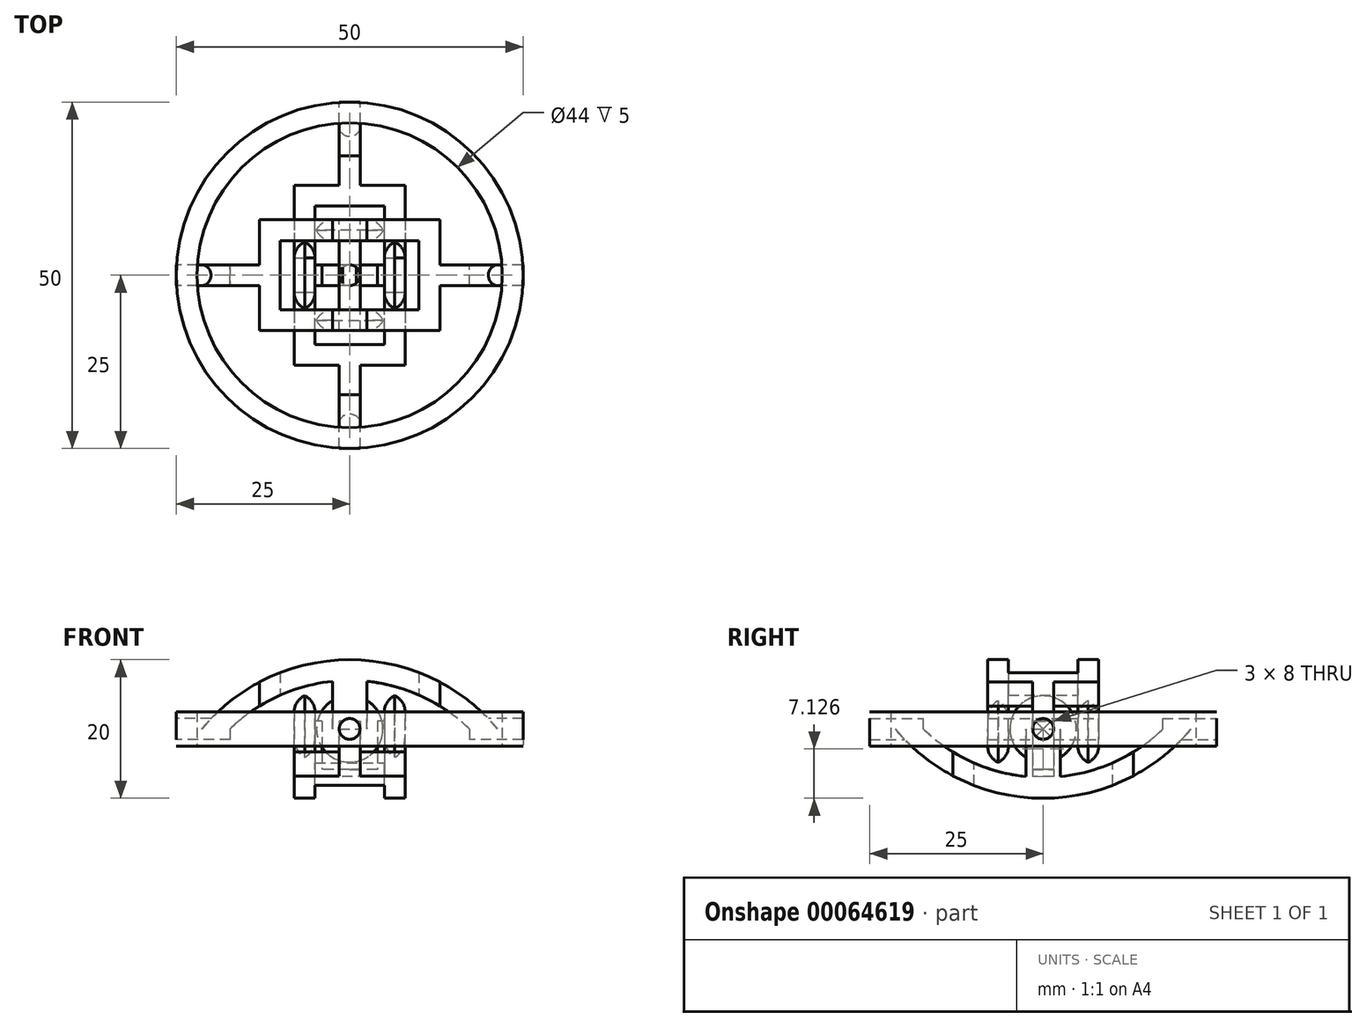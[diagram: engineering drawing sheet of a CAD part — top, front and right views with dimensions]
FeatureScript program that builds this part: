
annotation { "Feature Type Name" : "Feature", "Feature Type Description" : "" }
export const myFeature = defineFeature(function(context is Context, id is Id, definition is map)
    precondition{}
    {
        {
            var Q0;
            Q0=qCreatedBy(makeId("Top.planeOp"),FACE);
            var sketch = newSketch(context, id + "F0", { "sketchPlane" : qUnion([Q0])});
            skLineSegment(sketch, "E0.rect.bottom", {"start": v(10, -5) * mm, "end": v(-10, -5) * mm});
            skLineSegment(sketch, "E0.rect.top", {"start": v(10, 5) * mm, "end": v(-10, 5) * mm});
            skLineSegment(sketch, "E0.rect.left", {"start": v(10, -5) * mm, "end": v(10, 5) * mm});
            skLineSegment(sketch, "E0.rect.right", {"start": v(-10, -5) * mm, "end": v(-10, 5) * mm});
            skPoint(sketch, "E0.rect.middle", {"position": v(0, 0) * mm});
            skLineSegment(sketch, "E1.rect.bottom", {"start": v(-13, 8) * mm, "end": v(13, 8) * mm});
            skLineSegment(sketch, "E1.rect.top", {"start": v(-13, -8) * mm, "end": v(13, -8) * mm});
            skLineSegment(sketch, "E1.rect.left", {"start": v(-13, 8) * mm, "end": v(-13, -8) * mm});
            skLineSegment(sketch, "E1.rect.right", {"start": v(13, 8) * mm, "end": v(13, -8) * mm});
            skLineSegment(sketch, "E2", {"start": v(-13, 1.5) * mm, "end": v(-28, 1.5) * mm});
            skLineSegment(sketch, "E3", {"start": v(-28, 1.5) * mm, "end": v(-28, -1.5) * mm});
            skLineSegment(sketch, "E4", {"start": v(-28, -1.5) * mm, "end": v(-13, -1.5) * mm});
            skLineSegment(sketch, "E5", {"start": v(13, -1.5) * mm, "end": v(28, -1.5) * mm});
            skLineSegment(sketch, "E6", {"start": v(28, -1.5) * mm, "end": v(28, 1.5) * mm});
            skLineSegment(sketch, "E7", {"start": v(28, 1.5) * mm, "end": v(13, 1.5) * mm});
            skSolve(sketch);
        }
        {
            var Q0;
            {var subQ0=sQuery(id+"F0.wireOp",EDGE,"E2");Q0=makeQuery(id+"F0.imprint","IMPRINT",FACE,{"disambiguationData":[TD([[makeQuery(id+"F0.imprint","IMPRINT",EDGE,{"derivedFrom":subQ0}),1.0]])]});}
            var Q1;
            Q1=makeQuery(id+"F0.imprint","IMPRINT",FACE,{"disambiguationData":[TD([[makeQuery(id+"F0.imprint","IMPRINT",EDGE,{"derivedFrom":sQuery(id+"F0.wireOp",EDGE,"E0.rect.bottom")}),1.0]])]});
            var Q2;
            {var subQ0=sQuery(id+"F0.wireOp",EDGE,"E5");Q2=makeQuery(id+"F0.imprint","IMPRINT",FACE,{"disambiguationData":[TD([[makeQuery(id+"F0.imprint","IMPRINT",EDGE,{"derivedFrom":subQ0}),1.0]])]});}
            extrude(context, id + "F1", {"entities" : qUnion([Q0, Q1, Q2]), "endBound" : BoundingType.SYMMETRIC, "depth" : 50 * mm});
        }
        {
            var Q0;
            Q0=qCreatedBy(makeId("Front.planeOp"),FACE);
            var sketch = newSketch(context, id + "F2", { "sketchPlane" : qUnion([Q0])});
            skLineSegment(sketch, "E8", {"start": v(0, 46.34) * mm, "end": v(0, -43.17) * mm});
            skSolve(sketch);
        }
        {
            var Q0;
            Q0=qCreatedBy(makeId("Front.planeOp"),FACE);
            var sketch = newSketch(context, id + "F3", { "sketchPlane" : qUnion([Q0])});
            skCircle(sketch, "E9", {"center": v(0, 0) * mm, "radius": 5 * mm});
            skArc(sketch, "E10", {"start": v(20, 1.5) * mm, "mid": v(10.87, 7.79) * mm, "end": v(0, 10) * mm});
            skArc(sketch, "E11.0", {"start": v(17.26, 0) * mm, "mid": v(10.46, 4.68) * mm, "end": v(2.5, 6.87) * mm});
            skLineSegment(sketch, "E12", {"start": v(25, 1.5) * mm, "end": v(25, 0) * mm});
            skLineSegment(sketch, "E13", {"start": v(20, 1.5) * mm, "end": v(25, 1.5) * mm});
            skLineSegment(sketch, "E14", {"start": v(2.5, 6.87) * mm, "end": v(2.5, 4.33) * mm});
            skLineSegment(sketch, "E15.MirrorCS", {"start": v(-25, 1.5) * mm, "end": v(-25, 0) * mm});
            skArc(sketch, "E16.MirrorCS", {"start": v(-20, 1.5) * mm, "mid": v(-10.87, 7.79) * mm, "end": v(0, 10) * mm});
            skLineSegment(sketch, "E17.MirrorCS", {"start": v(-2.5, 6.87) * mm, "end": v(-2.5, 4.33) * mm});
            skArc(sketch, "E18.MirrorCS", {"start": v(-17.26, 0) * mm, "mid": v(-10.46, 4.68) * mm, "end": v(-2.5, 6.87) * mm});
            skLineSegment(sketch, "E19.MirrorCS", {"start": v(-20, 1.5) * mm, "end": v(-25, 1.5) * mm});
            skLineSegment(sketch, "E20", {"start": v(17.26, 0) * mm, "end": v(17.26, -1.5) * mm});
            skLineSegment(sketch, "E21", {"start": v(17.26, -1.5) * mm, "end": v(25, -1.5) * mm});
            skLineSegment(sketch, "E22", {"start": v(25, -1.5) * mm, "end": v(25, 0) * mm});
            skLineSegment(sketch, "E23", {"start": v(-25, 0) * mm, "end": v(-25, -1.5) * mm});
            skLineSegment(sketch, "E24", {"start": v(-25, -1.5) * mm, "end": v(-17.26, -1.5) * mm});
            skLineSegment(sketch, "E25", {"start": v(-17.26, -1.5) * mm, "end": v(-17.26, 0) * mm});
            skLineSegment(sketch, "E26", {"start": v(0, 10) * mm, "end": v(0, 0) * mm, "construction": true});
            skSolve(sketch);
        }
        {
            var Q0;
            Q0=makeQuery(id+"F3.imprint","IMPRINT",FACE,{"disambiguationData":[TD([[makeQuery(id+"F3.imprint","IMPRINT",EDGE,{"derivedFrom":sQuery(id+"F3.wireOp",EDGE,"E10")}),1.0]])]});
            var Q1;
            {var subQ0=sQuery(id+"F3.wireOp",EDGE,"E9");var subQ1=makeQuery(id+"F3.imprint","INTERSECT",VERTEX,{"derivedFrom":[subQ0,sQuery(id+"F3.wireOp",EDGE,"E14")]});Q1=makeQuery(id+"F3.imprint","IMPRINT",FACE,{"disambiguationData":[TD([[makeQuery(id+"F3.imprint","IMPRINT",EDGE,{"disambiguationData":[TD([[subQ1,-1.0]])],"derivedFrom":subQ0}),1.0]])]});}
            var Q2;
            Q2=makeQuery(id+"F3.imprint","IMPRINT",FACE,{"disambiguationData":[TD([[makeQuery(id+"F3.imprint","IMPRINT",EDGE,{"derivedFrom":sQuery(id+"F3.wireOp",EDGE,"7cc19d34-6d25-45fe-b9ab-7269c0df2a4a4.MirrorCS")}),-1.0]])]});
            var Q3;
            Q3=makeQuery(id+"F3.imprint","IMPRINT",FACE,{"disambiguationData":[TD([[makeQuery(id+"F3.imprint","IMPRINT",EDGE,{"derivedFrom":sQuery(id+"F3.wireOp",EDGE,"Re02jO8j-83i6-SrPj-ZhnU-ibMTVgBzKa9t")}),1.0]])]});
            extrude(context, id + "F4", {"entities" : qUnion([Q0, Q1, Q2, Q3]), "endBound" : BoundingType.THROUGH_ALL, "depth" : 25 * mm, "hasSecondDirection" : true, "secondDirectionBound" : SecondDirectionBoundingType.THROUGH_ALL, "secondDirectionOppositeDirection" : true, "secondDirectionDepth" : 25 * mm});
        }
        {
            var Q0;
            Q0=makeQuery(id+"F1.opExtrude","SWEPT_BODY",BODY,{"disambiguationData":[OSD([sQuery(id+"F0.wireOp",EDGE,"E0.rect.bottom"),sQuery(id+"F0.wireOp",EDGE,"E0.rect.top"),sQuery(id+"F0.wireOp",EDGE,"E0.rect.left"),sQuery(id+"F0.wireOp",EDGE,"E0.rect.right"),sQuery(id+"F0.wireOp",EDGE,"E1.rect.bottom"),sQuery(id+"F0.wireOp",EDGE,"E1.rect.top"),sQuery(id+"F0.wireOp",EDGE,"E1.rect.left"),sQuery(id+"F0.wireOp",EDGE,"E1.rect.right"),sQuery(id+"F0.wireOp",EDGE,"E2"),sQuery(id+"F0.wireOp",EDGE,"E3"),sQuery(id+"F0.wireOp",EDGE,"E4"),sQuery(id+"F0.wireOp",EDGE,"E5"),sQuery(id+"F0.wireOp",EDGE,"E6"),sQuery(id+"F0.wireOp",EDGE,"E7")])]});
            var Q1;
            Q1=makeQuery(id+"F4.opExtrude","SWEPT_BODY",BODY,{"disambiguationData":[OSD([sQuery(id+"F3.wireOp",EDGE,"E9"),sQuery(id+"F3.wireOp",EDGE,"E10"),sQuery(id+"F3.wireOp",EDGE,"E11.0"),sQuery(id+"F3.wireOp",EDGE,"E12"),sQuery(id+"F3.wireOp",EDGE,"Re02jO8j-83i6-SrPj-ZhnU-ibMTVgBzKa9t"),sQuery(id+"F3.wireOp",EDGE,"E13"),sQuery(id+"F3.wireOp",EDGE,"E14"),sQuery(id+"F3.wireOp",EDGE,"E15.MirrorCS"),sQuery(id+"F3.wireOp",EDGE,"E16.MirrorCS"),sQuery(id+"F3.wireOp",EDGE,"E17.MirrorCS"),sQuery(id+"F3.wireOp",EDGE,"E18.MirrorCS"),sQuery(id+"F3.wireOp",EDGE,"7cc19d34-6d25-45fe-b9ab-7269c0df2a4a4.MirrorCS"),sQuery(id+"F3.wireOp",EDGE,"E19.MirrorCS")])]});
            booleanBodies(context, id + "F5", {"operationType" : BooleanOperationType.INTERSECTION, "tools" : qUnion([Q0, Q1])});
        }
        {
            var Q0;
            Q0=makeQuery(id+"F5.opBoolean","INTERSECT",EDGE,{"derivedFrom":[makeQuery(id+"F1.opExtrude","SWEPT_FACE",FACE,{"disambiguationData":[OSD([sQuery(id+"F0.wireOp",EDGE,"E4")])]}),makeQuery(id+"F4.opExtrude","SWEPT_FACE",FACE,{"disambiguationData":[OSD([sQuery(id+"F3.wireOp",EDGE,"E19.MirrorCS")])]})]});
            var Q1;
            Q1=makeQuery(id+"F5.opBoolean","INTERSECT",EDGE,{"derivedFrom":[makeQuery(id+"F1.opExtrude","SWEPT_FACE",FACE,{"disambiguationData":[OSD([sQuery(id+"F0.wireOp",EDGE,"E2")])]}),makeQuery(id+"F4.opExtrude","SWEPT_FACE",FACE,{"disambiguationData":[OSD([sQuery(id+"F3.wireOp",EDGE,"E19.MirrorCS")])]})]});
            var Q2;
            Q2=makeQuery(id+"F5.opBoolean","INTERSECT",EDGE,{"derivedFrom":[makeQuery(id+"F1.opExtrude","SWEPT_FACE",FACE,{"disambiguationData":[OSD([sQuery(id+"F0.wireOp",EDGE,"E4")])]}),makeQuery(id+"F4.opExtrude","SWEPT_FACE",FACE,{"disambiguationData":[OSD([sQuery(id+"F3.wireOp",EDGE,"E24")])]})]});
            var Q3;
            Q3=makeQuery(id+"F5.opBoolean","INTERSECT",EDGE,{"derivedFrom":[makeQuery(id+"F1.opExtrude","SWEPT_FACE",FACE,{"disambiguationData":[OSD([sQuery(id+"F0.wireOp",EDGE,"E2")])]}),makeQuery(id+"F4.opExtrude","SWEPT_FACE",FACE,{"disambiguationData":[OSD([sQuery(id+"F3.wireOp",EDGE,"E24")])]})]});
            var Q4;
            Q4=makeQuery(id+"F5.opBoolean","INTERSECT",EDGE,{"derivedFrom":[makeQuery(id+"F1.opExtrude","SWEPT_FACE",FACE,{"disambiguationData":[OSD([sQuery(id+"F0.wireOp",EDGE,"E7")])]}),makeQuery(id+"F4.opExtrude","SWEPT_FACE",FACE,{"disambiguationData":[OSD([sQuery(id+"F3.wireOp",EDGE,"E13")])]})]});
            var Q5;
            Q5=makeQuery(id+"F5.opBoolean","INTERSECT",EDGE,{"derivedFrom":[makeQuery(id+"F1.opExtrude","SWEPT_FACE",FACE,{"disambiguationData":[OSD([sQuery(id+"F0.wireOp",EDGE,"E7")])]}),makeQuery(id+"F4.opExtrude","SWEPT_FACE",FACE,{"disambiguationData":[OSD([sQuery(id+"F3.wireOp",EDGE,"E21")])]})]});
            var Q6;
            Q6=makeQuery(id+"F5.opBoolean","INTERSECT",EDGE,{"derivedFrom":[makeQuery(id+"F1.opExtrude","SWEPT_FACE",FACE,{"disambiguationData":[OSD([sQuery(id+"F0.wireOp",EDGE,"E5")])]}),makeQuery(id+"F4.opExtrude","SWEPT_FACE",FACE,{"disambiguationData":[OSD([sQuery(id+"F3.wireOp",EDGE,"E21")])]})]});
            var Q7;
            Q7=makeQuery(id+"F5.opBoolean","INTERSECT",EDGE,{"derivedFrom":[makeQuery(id+"F1.opExtrude","SWEPT_FACE",FACE,{"disambiguationData":[OSD([sQuery(id+"F0.wireOp",EDGE,"E5")])]}),makeQuery(id+"F4.opExtrude","SWEPT_FACE",FACE,{"disambiguationData":[OSD([sQuery(id+"F3.wireOp",EDGE,"E13")])]})]});
            fillet(context, id + "F6", {"entities" : qUnion([Q0, Q1, Q2, Q3, Q4, Q5, Q6, Q7]), "radius" : 1.5 * mm, "tangentPropagation" : true, "allowEdgeOverflow" : false});
        }
        {
            var Q0;
            Q0=makeQuery(id+"F8.opPattern","COPY",BODY,{"derivedFrom":makeQuery(id+"F5.opBoolean","INTERSECT",BODY,{"derivedFrom":[makeQuery(id+"F1.opExtrude","SWEPT_BODY",BODY,{"disambiguationData":[OSD([sQuery(id+"F0.wireOp",EDGE,"E0.rect.bottom"),sQuery(id+"F0.wireOp",EDGE,"E0.rect.top"),sQuery(id+"F0.wireOp",EDGE,"E0.rect.left"),sQuery(id+"F0.wireOp",EDGE,"E0.rect.right"),sQuery(id+"F0.wireOp",EDGE,"E1.rect.bottom"),sQuery(id+"F0.wireOp",EDGE,"E1.rect.top"),sQuery(id+"F0.wireOp",EDGE,"E1.rect.left"),sQuery(id+"F0.wireOp",EDGE,"E1.rect.right"),sQuery(id+"F0.wireOp",EDGE,"E2"),sQuery(id+"F0.wireOp",EDGE,"E3"),sQuery(id+"F0.wireOp",EDGE,"E4"),sQuery(id+"F0.wireOp",EDGE,"E5"),sQuery(id+"F0.wireOp",EDGE,"E6"),sQuery(id+"F0.wireOp",EDGE,"E7")])]}),makeQuery(id+"F4.opExtrude","SWEPT_BODY",BODY,{"disambiguationData":[OSD([sQuery(id+"F3.wireOp",EDGE,"2aad1849-a985-4e84-b269-a40025c45bef"),sQuery(id+"F3.wireOp",EDGE,"oUIs2XOa-4Vu7-z26a-mpJD-XDpxixJXROpf"),sQuery(id+"F3.wireOp",EDGE,"nCIHGx5T-ErFx-Tt1R-lAtw-DeMqCE7hFv12"),sQuery(id+"F3.wireOp",EDGE,"2f387838-2f8b-4cff-a27e-d127b03e8324.0"),sQuery(id+"F3.wireOp",EDGE,"2f387838-2f8b-4cff-a27e-d127b03e8324.1"),sQuery(id+"F3.wireOp",EDGE,"2f387838-2f8b-4cff-a27e-d127b03e8324.2"),sQuery(id+"F3.wireOp",EDGE,"2f387838-2f8b-4cff-a27e-d127b03e8324.3"),sQuery(id+"F3.wireOp",EDGE,"2f387838-2f8b-4cff-a27e-d127b03e8324.4")])]})]}),"instanceName":"1"});
            var Q1;
            Q1=makeQuery(id+"F5.opBoolean","INTERSECT",BODY,{"derivedFrom":[makeQuery(id+"F1.opExtrude","SWEPT_BODY",BODY,{"disambiguationData":[OSD([sQuery(id+"F0.wireOp",EDGE,"E0.rect.bottom"),sQuery(id+"F0.wireOp",EDGE,"E0.rect.top"),sQuery(id+"F0.wireOp",EDGE,"E0.rect.left"),sQuery(id+"F0.wireOp",EDGE,"E0.rect.right"),sQuery(id+"F0.wireOp",EDGE,"E1.rect.bottom"),sQuery(id+"F0.wireOp",EDGE,"E1.rect.top"),sQuery(id+"F0.wireOp",EDGE,"E1.rect.left"),sQuery(id+"F0.wireOp",EDGE,"E1.rect.right"),sQuery(id+"F0.wireOp",EDGE,"E2"),sQuery(id+"F0.wireOp",EDGE,"E3"),sQuery(id+"F0.wireOp",EDGE,"E4"),sQuery(id+"F0.wireOp",EDGE,"E5"),sQuery(id+"F0.wireOp",EDGE,"E6"),sQuery(id+"F0.wireOp",EDGE,"E7")])]}),makeQuery(id+"F4.opExtrude","SWEPT_BODY",BODY,{"disambiguationData":[OSD([sQuery(id+"F3.wireOp",EDGE,"E9"),sQuery(id+"F3.wireOp",EDGE,"E10"),sQuery(id+"F3.wireOp",EDGE,"E11.0"),sQuery(id+"F3.wireOp",EDGE,"E12"),sQuery(id+"F3.wireOp",EDGE,"E13"),sQuery(id+"F3.wireOp",EDGE,"E14"),sQuery(id+"F3.wireOp",EDGE,"E15.MirrorCS"),sQuery(id+"F3.wireOp",EDGE,"E16.MirrorCS"),sQuery(id+"F3.wireOp",EDGE,"E17.MirrorCS"),sQuery(id+"F3.wireOp",EDGE,"E18.MirrorCS"),sQuery(id+"F3.wireOp",EDGE,"E19.MirrorCS"),sQuery(id+"F3.wireOp",EDGE,"E20"),sQuery(id+"F3.wireOp",EDGE,"E21"),sQuery(id+"F3.wireOp",EDGE,"E22"),sQuery(id+"F3.wireOp",EDGE,"E23"),sQuery(id+"F3.wireOp",EDGE,"E24"),sQuery(id+"F3.wireOp",EDGE,"E25")])]})]});
            var Q2;
            Q2=qCreatedBy(makeId("Top.planeOp"),FACE);
            mirror(context, id + "F7", {"entities" : qUnion([Q0, Q1]), "mirrorPlane" : qUnion([Q2])});
        }
        {
            var Q0;
            Q0=makeQuery(id+"F7.opPattern","COPY",BODY,{"derivedFrom":makeQuery(id+"F5.opBoolean","INTERSECT",BODY,{"derivedFrom":[makeQuery(id+"F1.opExtrude","SWEPT_BODY",BODY,{"disambiguationData":[OSD([sQuery(id+"F0.wireOp",EDGE,"E0.rect.bottom"),sQuery(id+"F0.wireOp",EDGE,"E0.rect.top"),sQuery(id+"F0.wireOp",EDGE,"E0.rect.left"),sQuery(id+"F0.wireOp",EDGE,"E0.rect.right"),sQuery(id+"F0.wireOp",EDGE,"E1.rect.bottom"),sQuery(id+"F0.wireOp",EDGE,"E1.rect.top"),sQuery(id+"F0.wireOp",EDGE,"E1.rect.left"),sQuery(id+"F0.wireOp",EDGE,"E1.rect.right"),sQuery(id+"F0.wireOp",EDGE,"E2"),sQuery(id+"F0.wireOp",EDGE,"E3"),sQuery(id+"F0.wireOp",EDGE,"E4"),sQuery(id+"F0.wireOp",EDGE,"E5"),sQuery(id+"F0.wireOp",EDGE,"E6"),sQuery(id+"F0.wireOp",EDGE,"E7")])]}),makeQuery(id+"F4.opExtrude","SWEPT_BODY",BODY,{"disambiguationData":[OSD([sQuery(id+"F3.wireOp",EDGE,"E9"),sQuery(id+"F3.wireOp",EDGE,"E10"),sQuery(id+"F3.wireOp",EDGE,"E11.0"),sQuery(id+"F3.wireOp",EDGE,"E12"),sQuery(id+"F3.wireOp",EDGE,"E13"),sQuery(id+"F3.wireOp",EDGE,"E14"),sQuery(id+"F3.wireOp",EDGE,"E15.MirrorCS"),sQuery(id+"F3.wireOp",EDGE,"E16.MirrorCS"),sQuery(id+"F3.wireOp",EDGE,"E17.MirrorCS"),sQuery(id+"F3.wireOp",EDGE,"E18.MirrorCS"),sQuery(id+"F3.wireOp",EDGE,"E19.MirrorCS"),sQuery(id+"F3.wireOp",EDGE,"E20"),sQuery(id+"F3.wireOp",EDGE,"E21"),sQuery(id+"F3.wireOp",EDGE,"E22"),sQuery(id+"F3.wireOp",EDGE,"E23"),sQuery(id+"F3.wireOp",EDGE,"E24"),sQuery(id+"F3.wireOp",EDGE,"E25")])]})]}),"instanceName":"1"});
            var Q1;
            Q1=sQuery(id+"F2.wireOp",EDGE,"E8");
            transform(context, id + "F8", {"entities" : qUnion([Q0]), "transformType" : TransformType.ROTATION, "transformAxis" : qUnion([Q1]), "angle" : 90 * degree, "makeCopy" : false});
        }
        {
            var Q0;
            Q0=makeQuery(id+"F7.opPattern","COPY",FACE,{"derivedFrom":makeQuery(id+"F4.opExtrude","SWEPT_FACE",FACE,{"disambiguationData":[OSD([sQuery(id+"F3.wireOp",EDGE,"E15.MirrorCS"),sQuery(id+"F3.wireOp",EDGE,"E23")])]}),"instanceName":"1"});
            var Q1;
            Q1=makeQuery(id+"F1.opExtrude","SWEPT_FACE",FACE,{"disambiguationData":[OSD([sQuery(id+"F0.wireOp",EDGE,"E1.rect.top")])]});
            var Q2;
            Q2=makeQuery(id+"F1.opExtrude","SWEPT_FACE",FACE,{"disambiguationData":[OSD([sQuery(id+"F0.wireOp",EDGE,"E1.rect.bottom")])]});
            extrude(context, id + "F9", {"entities" : qUnion([Q0]), "endBound" : BoundingType.UP_TO_SURFACE, "oppositeDirection" : true, "endBoundEntityFace" : qUnion([Q1]), "depth" : 25 * mm, "hasSecondDirection" : true, "secondDirectionBound" : SecondDirectionBoundingType.UP_TO_SURFACE, "secondDirectionOppositeDirection" : true, "secondDirectionBoundEntityFace" : qUnion([Q2]), "secondDirectionDepth" : 25 * mm});
        }
        {
            var Q0;
            {var subQ0=sQuery(id+"F3.wireOp",EDGE,"E11.0");var subQ1=sQuery(id+"F3.wireOp",EDGE,"E14");Q0=makeQuery(id+"F7.opPattern","COPY",EDGE,{"derivedFrom":makeQuery(id+"F5.opBoolean","SPLIT",EDGE,{"disambiguationData":[TD([makeQuery(id+"F1.opExtrude","SWEPT_FACE",FACE,{"disambiguationData":[OSD([sQuery(id+"F0.wireOp",EDGE,"E0.rect.top")])]})])],"derivedFrom":makeQuery(id+"F4.opExtrude","SWEPT_EDGE",EDGE,{"disambiguationData":[OSD([subQ0,subQ1])]})}),"instanceName":"1"});}
            cPlane(context, id + "F10", {"entities" : qUnion([Q0]), "cplaneType" : CPlaneType.LINE_ANGLE, "offset" : 150 * mm, "angle" : 90 * degree, "width" : 150 * mm, "height" : 150 * mm});
        }
        {
            var Q0;
            Q0=qCreatedBy(id+"F10.planeOp",FACE);
            var sketch = newSketch(context, id + "F11", { "sketchPlane" : qUnion([Q0])});
            skCircle(sketch, "E27", {"center": v(0, 0) * mm, "radius": 1.5 * mm});
            skLineSegment(sketch, "E28.rect.bottom", {"start": v(5, 1.5) * mm, "end": v(-5, 1.5) * mm});
            skLineSegment(sketch, "E28.rect.top", {"start": v(5, -1.5) * mm, "end": v(-5, -1.5) * mm});
            skLineSegment(sketch, "E28.rect.left", {"start": v(5, 1.5) * mm, "end": v(5, -1.5) * mm});
            skLineSegment(sketch, "E28.rect.right", {"start": v(-5, 1.5) * mm, "end": v(-5, -1.5) * mm});
            skLineSegment(sketch, "E29", {"start": v(-4, -1.5) * mm, "end": v(-4, 1.5) * mm});
            skLineSegment(sketch, "E30", {"start": v(4, 1.5) * mm, "end": v(4, -1.5) * mm});
            skSolve(sketch);
        }
        {
            var Q0;
            {var subQ0=sQuery(id+"F11.wireOp",EDGE,"E28.rect.left");Q0=makeQuery(id+"F11.imprint","IMPRINT",FACE,{"disambiguationData":[TD([[makeQuery(id+"F11.imprint","IMPRINT",EDGE,{"derivedFrom":subQ0}),-1.0]])]});}
            var Q1;
            {var subQ0=sQuery(id+"F11.wireOp",EDGE,"E27");var subQ1=makeQuery(id+"F11.imprint","INTERSECT",VERTEX,{"derivedFrom":[subQ0,sQuery(id+"F11.wireOp",EDGE,"E28.rect.bottom")]});Q1=makeQuery(id+"F11.imprint","IMPRINT",FACE,{"disambiguationData":[TD([[makeQuery(id+"F11.imprint","IMPRINT",EDGE,{"disambiguationData":[TD([[subQ1,-1.0]])],"derivedFrom":subQ0}),1.0]])]});}
            var Q2;
            {var subQ0=sQuery(id+"F11.wireOp",EDGE,"E28.rect.right");Q2=makeQuery(id+"F11.imprint","IMPRINT",FACE,{"disambiguationData":[TD([[makeQuery(id+"F11.imprint","IMPRINT",EDGE,{"derivedFrom":subQ0}),1.0]])]});}
            var Q3;
            {var subQ5=sQuery(id+"F11.wireOp",EDGE,"E30");Q3=makeQuery(id+"F11.imprint","IMPRINT",FACE,{"disambiguationData":[TD([[makeQuery(id+"F11.imprint","IMPRINT",EDGE,{"derivedFrom":subQ5}),-1.0]])]});}
            var Q4;
            {var subQ5=sQuery(id+"F11.wireOp",EDGE,"E29");Q4=makeQuery(id+"F11.imprint","IMPRINT",FACE,{"disambiguationData":[TD([[makeQuery(id+"F11.imprint","IMPRINT",EDGE,{"derivedFrom":subQ5}),-1.0]])]});}
            extrude(context, id + "F12", {"entities" : qUnion([Q0, Q1, Q2, Q3, Q4]), "depth" : 1 * mm});
        }
        {
            var Q0;
            {var subQ0=sQuery(id+"F11.wireOp",EDGE,"E27");var subQ1=makeQuery(id+"F11.imprint","INTERSECT",VERTEX,{"derivedFrom":[subQ0,sQuery(id+"F11.wireOp",EDGE,"E28.rect.bottom")]});Q0=makeQuery(id+"F11.imprint","IMPRINT",FACE,{"disambiguationData":[TD([[makeQuery(id+"F11.imprint","IMPRINT",EDGE,{"disambiguationData":[TD([[subQ1,-1.0]])],"derivedFrom":subQ0}),1.0]])]});}
            var Q1;
            {var subQ0=sQuery(id+"F11.wireOp",EDGE,"E28.rect.right");Q1=makeQuery(id+"F11.imprint","IMPRINT",FACE,{"disambiguationData":[TD([[makeQuery(id+"F11.imprint","IMPRINT",EDGE,{"derivedFrom":subQ0}),1.0]])]});}
            var Q2;
            {var subQ0=sQuery(id+"F11.wireOp",EDGE,"E28.rect.left");Q2=makeQuery(id+"F11.imprint","IMPRINT",FACE,{"disambiguationData":[TD([[makeQuery(id+"F11.imprint","IMPRINT",EDGE,{"derivedFrom":subQ0}),-1.0]])]});}
            var Q3;
            Q3=makeQuery(id+"F9.opExtrude","SWEPT_FACE",FACE,{"disambiguationData":[OSD([sQuery(id+"F0.wireOp",EDGE,"E2"),sQuery(id+"F3.wireOp",EDGE,"E15.MirrorCS"),sQuery(id+"F3.wireOp",EDGE,"E23"),sQuery(id+"F3.wireOp",EDGE,"E24")])]});
            var Q4;
            Q4=makeQuery(id+"F9.opExtrude","SWEPT_BODY",BODY,{"disambiguationData":[OSD([sQuery(id+"F3.wireOp",EDGE,"E15.MirrorCS"),sQuery(id+"F3.wireOp",EDGE,"E23")])]});
            extrude(context, id + "F13", {"entities" : qUnion([Q0, Q1, Q2]), "operationType" : NewBodyOperationType.ADD, "endBoundEntityFace" : qUnion([Q3]), "endBoundEntityBody" : qUnion([Q4]), "depth" : 8 * mm});
        }
        {
            var Q0;
            Q0=qCreatedBy(makeId("Top.planeOp"),FACE);
            var sketch = newSketch(context, id + "F14", { "sketchPlane" : qUnion([Q0])});
            skCircle(sketch, "E31", {"center": v(0, 0) * mm, "radius": 25 * mm});
            skCircle(sketch, "E32.0", {"center": v(0, 0) * mm, "radius": 22 * mm});
            skSolve(sketch);
        }
        {
            var Q0;
            Q0=makeQuery(id+"F14.imprint","IMPRINT",FACE,{"disambiguationData":[TD([[makeQuery(id+"F14.imprint","IMPRINT",EDGE,{"derivedFrom":sQuery(id+"F14.wireOp",EDGE,"E31")}),1.0]])]});
            extrude(context, id + "F15", {"entities" : qUnion([Q0]), "endBound" : BoundingType.SYMMETRIC, "depth" : 5 * mm});
        }
        {
            var Q0;
            Q0=makeQuery(id+"F7.opPattern","COPY",EDGE,{"derivedFrom":makeQuery(id+"F5.opBoolean","INTERSECT",EDGE,{"derivedFrom":[makeQuery(id+"F1.opExtrude","SWEPT_FACE",FACE,{"disambiguationData":[OSD([sQuery(id+"F0.wireOp",EDGE,"E0.rect.bottom")])]}),makeQuery(id+"F4.opExtrude","SWEPT_FACE",FACE,{"disambiguationData":[OSD([sQuery(id+"F3.wireOp",EDGE,"E9")])]})]}),"instanceName":"1"});
            var Q1;
            Q1=makeQuery(id+"F7.opPattern","COPY",EDGE,{"derivedFrom":makeQuery(id+"F5.opBoolean","INTERSECT",EDGE,{"derivedFrom":[makeQuery(id+"F1.opExtrude","SWEPT_FACE",FACE,{"disambiguationData":[OSD([sQuery(id+"F0.wireOp",EDGE,"E0.rect.top")])]}),makeQuery(id+"F4.opExtrude","SWEPT_FACE",FACE,{"disambiguationData":[OSD([sQuery(id+"F3.wireOp",EDGE,"E9")])]})]}),"instanceName":"1"});
            var Q2;
            Q2=makeQuery(id+"F5.opBoolean","INTERSECT",EDGE,{"derivedFrom":[makeQuery(id+"F1.opExtrude","SWEPT_FACE",FACE,{"disambiguationData":[OSD([sQuery(id+"F0.wireOp",EDGE,"E0.rect.bottom")])]}),makeQuery(id+"F4.opExtrude","SWEPT_FACE",FACE,{"disambiguationData":[OSD([sQuery(id+"F3.wireOp",EDGE,"E9")])]})]});
            var Q3;
            Q3=makeQuery(id+"F5.opBoolean","INTERSECT",EDGE,{"derivedFrom":[makeQuery(id+"F1.opExtrude","SWEPT_FACE",FACE,{"disambiguationData":[OSD([sQuery(id+"F0.wireOp",EDGE,"E0.rect.top")])]}),makeQuery(id+"F4.opExtrude","SWEPT_FACE",FACE,{"disambiguationData":[OSD([sQuery(id+"F3.wireOp",EDGE,"E9")])]})]});
            var Q4;
            Q4=makeQuery(id+"F5.opBoolean","INTERSECT",EDGE,{"derivedFrom":[makeQuery(id+"F1.opExtrude","SWEPT_FACE",FACE,{"disambiguationData":[OSD([sQuery(id+"F0.wireOp",EDGE,"E1.rect.top")])]}),makeQuery(id+"F4.opExtrude","SWEPT_FACE",FACE,{"disambiguationData":[OSD([sQuery(id+"F3.wireOp",EDGE,"E9")])]})]});
            var Q5;
            Q5=makeQuery(id+"F7.opPattern","COPY",EDGE,{"derivedFrom":makeQuery(id+"F5.opBoolean","INTERSECT",EDGE,{"derivedFrom":[makeQuery(id+"F1.opExtrude","SWEPT_FACE",FACE,{"disambiguationData":[OSD([sQuery(id+"F0.wireOp",EDGE,"E1.rect.top")])]}),makeQuery(id+"F4.opExtrude","SWEPT_FACE",FACE,{"disambiguationData":[OSD([sQuery(id+"F3.wireOp",EDGE,"E9")])]})]}),"instanceName":"1"});
            var Q6;
            Q6=makeQuery(id+"F5.opBoolean","INTERSECT",EDGE,{"derivedFrom":[makeQuery(id+"F1.opExtrude","SWEPT_FACE",FACE,{"disambiguationData":[OSD([sQuery(id+"F0.wireOp",EDGE,"E1.rect.bottom")])]}),makeQuery(id+"F4.opExtrude","SWEPT_FACE",FACE,{"disambiguationData":[OSD([sQuery(id+"F3.wireOp",EDGE,"E9")])]})]});
            var Q7;
            Q7=makeQuery(id+"F7.opPattern","COPY",EDGE,{"derivedFrom":makeQuery(id+"F5.opBoolean","INTERSECT",EDGE,{"derivedFrom":[makeQuery(id+"F1.opExtrude","SWEPT_FACE",FACE,{"disambiguationData":[OSD([sQuery(id+"F0.wireOp",EDGE,"E1.rect.bottom")])]}),makeQuery(id+"F4.opExtrude","SWEPT_FACE",FACE,{"disambiguationData":[OSD([sQuery(id+"F3.wireOp",EDGE,"E9")])]})]}),"instanceName":"1"});
            fillet(context, id + "F16", {"entities" : qUnion([Q0, Q1, Q2, Q3, Q4, Q5, Q6, Q7]), "radius" : 2.5 * mm, "tangentPropagation" : true, "allowEdgeOverflow" : false});
        }
    });
